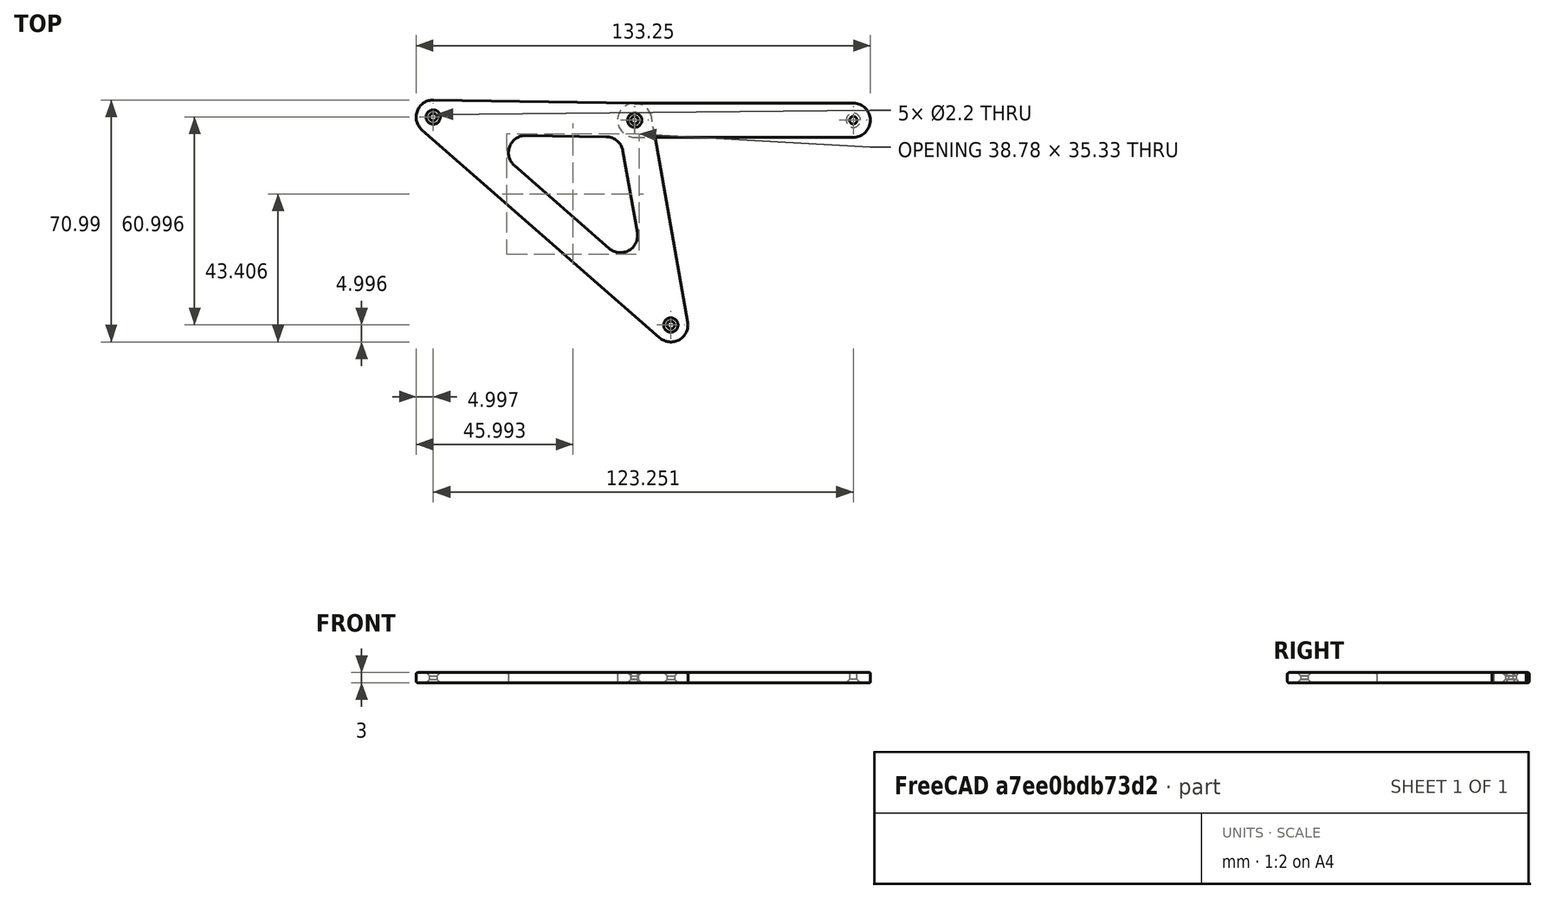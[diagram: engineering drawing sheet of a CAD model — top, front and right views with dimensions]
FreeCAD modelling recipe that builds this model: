
FCSTD DOCUMENT  (FreeCAD 0.20R)
Label: Support
License: All rights reserved
LicenseURL: http://en.wikipedia.org/wiki/All_rights_reserved
objects: Sketcher::SketchObject×2, PartDesign::Pad×2, PartDesign::Chamfer×2, PartDesign::Fillet×2, PartDesign::Body×2
note: 16 computed .brp shape members not serialized (recipe doc carries the construction recipe); baked Part::Feature solids carry a one-line shape summary decoded from their .brp

FEATURE [Sketcher::SketchObject] Sketch
  FullyConstrained = true
  MapMode = 5
  Support = -> [XY_Plane]
  sketch-geometry (6):
    g0: ArcOfCircle CenterX=0 CenterY=0 CenterZ=0 NormalX=0 NormalY=0 NormalZ=1 AngleXU=0 Radius=5 StartAngle=1.5708 EndAngle=4.71239
    g1: ArcOfCircle CenterX=64.168 CenterY=0 CenterZ=0 NormalX=0 NormalY=0 NormalZ=1 AngleXU=0 Radius=5 StartAngle=4.71239 EndAngle=7.85398
    g2: LineSegment StartX=-4.53e-14 StartY=-5 StartZ=0 EndX=64.168 EndY=-5 EndZ=0
    g3: LineSegment StartX=64.168 StartY=5 StartZ=0 EndX=-4.26e-14 EndY=5 EndZ=0
    g4: Circle CenterX=0 CenterY=0 CenterZ=0 NormalX=0 NormalY=0 NormalZ=1 AngleXU=0 Radius=1.1
    g5: Circle CenterX=64.168 CenterY=0 CenterZ=0 NormalX=0 NormalY=0 NormalZ=1 AngleXU=0 Radius=1.1
  constraints (13):
    c: Tangent(g0,g2) = -1.5708
    c: Tangent(g2,g1) = -1.5708
    c: Tangent(g1,g3) = -1.5708
    c: Tangent(g3,g0) = -1.5708
    c: Equal(g0,g1)
    c: Horizontal(g1,g0)
    c: Distance(g0,g0) = 5
    c: Distance(g0,g1) = 64.168
    c: Coincident(g0,g-1)
    c: Coincident(g4,g0)
    c: Diameter(g4) = 2.2
    c: Coincident(g5,g1)
    c: Diameter(g5) = 2.2
FEATURE [PartDesign::Pad] Pad
  Direction = (0,0,1)
  Length = 3
  Length2 = 10
  Profile = -> Sketch
  ReferenceAxis = -> Sketch [N_Axis]
  Type = 0
FEATURE [PartDesign::Chamfer] Chamfer
  Angle = 45
  Base = -> Pad [Edge17,Edge14]
  BaseFeature = -> Pad
  ChamferType = 0
  FlipDirection = false
  Size = 1
  Size2 = 1
  SupportTransform = false
  UseAllEdges = false
FEATURE [PartDesign::Fillet] Fillet
  Base = -> Chamfer [Edge1,Edge3,Edge4,Edge6,Edge7,Edge8,Edge9,Edge10,Edge12,Edge13,Edge14,Edge15,Edge16,Edge17,Edge18,Edge19,Edge20,Edge22]
  BaseFeature = -> Chamfer
  Radius = 0.3
  SupportTransform = false
  UseAllEdges = false
FEATURE [PartDesign::Body] Body  label="s1"
  Group = -> [Sketch,Pad,Chamfer,Fillet]
  Origin = -> Origin
  Tip = -> Fillet
FEATURE [Sketcher::SketchObject] Sketch001
  FullyConstrained = false
  sketch-geometry (15):
    g0: ArcOfCircle CenterX=-31.9855 CenterY=-9.49009 CenterZ=0 NormalX=0 NormalY=0 NormalZ=1 AngleXU=0 Radius=5 StartAngle=1.55525 EndAngle=3.99355
    g1: Circle CenterX=-59.0827 CenterY=0.932462 CenterZ=0 NormalX=0 NormalY=0 NormalZ=-1 AngleXU=0 Radius=1.1
    g2: Circle CenterX=0.0334442 CenterY=0.0132357 CenterZ=0 NormalX=0 NormalY=0 NormalZ=-1 AngleXU=0 Radius=1.1
    g3: Circle CenterX=10.6267 CenterY=-60.0639 CenterZ=0 NormalX=0 NormalY=0 NormalZ=-1 AngleXU=0 Radius=1.1
    g4: ArcOfCircle CenterX=0.0334442 CenterY=0.0132357 CenterZ=0 NormalX=0 NormalY=0 NormalZ=1 AngleXU=0 Radius=5 StartAngle=0.174533 EndAngle=1.55525
    g5: LineSegment StartX=0.111182 StartY=5.01263 StartZ=0 EndX=-59.005 EndY=5.93186 EndZ=0
    g6: ArcOfCircle CenterX=-59.0827 CenterY=0.932462 CenterZ=0 NormalX=0 NormalY=0 NormalZ=1 AngleXU=0 Radius=5 StartAngle=1.55525 EndAngle=3.99355
    g7: LineSegment StartX=15.5507 StartY=-59.1956 StartZ=0 EndX=4.95748 EndY=0.881477 EndZ=0
    g8: LineSegment StartX=-62.3753 StartY=-2.8304 StartZ=0 EndX=7.33412 EndY=-63.8267 EndZ=0
    g9: ArcOfCircle CenterX=10.6267 CenterY=-60.0639 CenterZ=0 NormalX=0 NormalY=0 NormalZ=1 AngleXU=0 Radius=5 StartAngle=3.99355 EndAngle=6.45772
    g10: ArcOfCircle CenterX=-4.15053 CenterY=-33.8459 CenterZ=0 NormalX=0 NormalY=0 NormalZ=1 AngleXU=0 Radius=5 StartAngle=3.99355 EndAngle=6.45772
    g11: LineSegment StartX=0.773504 StartY=-32.9777 StartZ=0 EndX=-3.45637 EndY=-8.9889 EndZ=0
    g12: ArcOfCircle CenterX=-8.38041 CenterY=-9.85714 CenterZ=0 NormalX=0 NormalY=0 NormalZ=1 AngleXU=0 Radius=5 StartAngle=0.174533 EndAngle=1.55525
    g13: LineSegment StartX=-8.30267 StartY=-4.85775 StartZ=0 EndX=-31.9078 EndY=-4.4907 EndZ=0
    g14: LineSegment StartX=-35.2781 StartY=-13.253 StartZ=0 EndX=-7.44308 EndY=-37.6088 EndZ=0
  constraints (2):
    c: Diameter(g2) = 2.2
    c: Equal(g1,g3)
FEATURE [PartDesign::Pad] Pad001
  Direction = (0,0,1)
  Length = 3
  Length2 = 10
  Profile = -> Sketch001
  ReferenceAxis = -> Sketch001 [N_Axis]
  Type = 0
FEATURE [PartDesign::Chamfer] Chamfer001
  Angle = 45
  Base = -> Pad001 [Edge38,Edge44,Edge41,Edge42,Edge39,Edge45]
  BaseFeature = -> Pad001
  ChamferType = 0
  FlipDirection = false
  Size = 1
  Size2 = 1
  SupportTransform = false
  UseAllEdges = false
FEATURE [PartDesign::Fillet] Fillet001
  Base = -> Chamfer001 [Edge26,Edge30,Edge13,Edge17]
  BaseFeature = -> Chamfer001
  Radius = 0.5
  SupportTransform = false
  UseAllEdges = false
FEATURE [PartDesign::Body] Body001  label="s2"
  Group = -> [Sketch001,Pad001,Chamfer001,Fillet001]
  Origin = -> Origin001
  Tip = -> Fillet001
